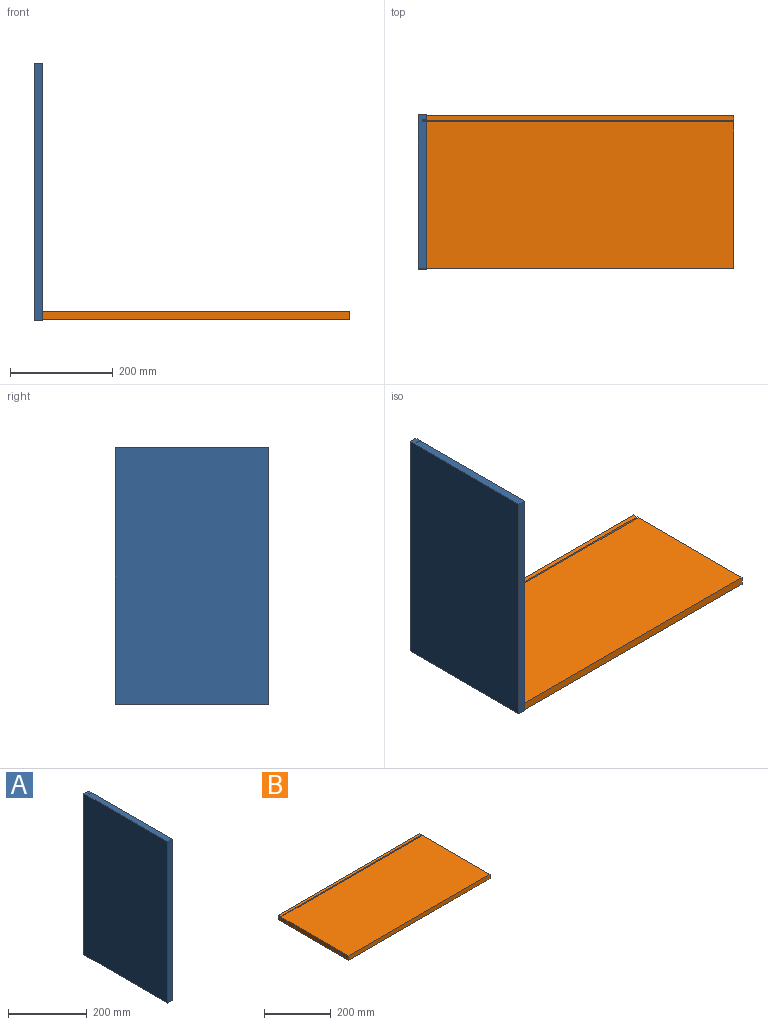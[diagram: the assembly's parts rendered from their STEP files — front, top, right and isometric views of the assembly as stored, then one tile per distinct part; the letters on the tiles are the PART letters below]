
ASSEMBLY  parts=2 mates=1
PART A: 18 faces, bbox 16x300x500 mm
  f0: plane 500x287mm, normal (1,0,0), area 143298.9mm2, adj f1,f3,f6,f8,f10,f12,f14,f16
  f1: plane 300x16mm, normal (0,0,-1), area 4776mm2, adj f0,f2,f4,f5,f6,f7,f8,f9
  f2: plane 500x10mm, normal (1,0,0), area 5000mm2, adj f1,f3,f5,f7
  f3: plane 300x16mm, normal (0,0,1), area 4776mm2, adj f0,f2,f4,f5,f6,f7,f8,f9
  f4: plane 500x300mm, normal (-1,0,0), area 150000mm2, adj f1,f3,f5,f6
  f5: plane 500x16mm, normal (0,1,0), area 8000mm2, adj f1,f2,f3,f4
  f6: plane 500x16mm, normal (0,-1,0), area 8000mm2, adj f0,f1,f3,f4
  f7: plane 500x8mm, normal (0,-1,0), area 4000mm2, adj f1,f2,f3,f9
  f8: plane 500x8mm, normal (0,1,0), area 4000mm2, adj f0,f1,f3,f9
  f9: plane 500x3mm, normal (1,0,0), area 1500mm2, adj f1,f3,f7,f8
  f10: cylinder r=4mm len=12mm, axis (1,0,0), area 301.6mm2, adj f0,f11
  f11: plane 8x8mm, normal (1,0,0), area 50.3mm2, adj f10
  f12: cylinder r=4mm len=12mm, axis (1,0,0), area 301.6mm2, adj f0,f13
  f13: plane 8x8mm, normal (1,0,0), area 50.3mm2, adj f12
  f14: cylinder r=4mm len=12mm, axis (1,0,0), area 301.6mm2, adj f0,f15
  f15: plane 8x8mm, normal (1,0,0), area 50.3mm2, adj f14
  f16: cylinder r=4mm len=12mm, axis (1,0,0), area 301.6mm2, adj f0,f17
  f17: plane 8x8mm, normal (1,0,0), area 50.3mm2, adj f16
PART B: 20 faces, bbox 600x299x16 mm
  f0: plane 600x9.5mm, normal (0,0,1), area 5700mm2, adj f1,f3,f5,f7
  f1: plane 299x16mm, normal (-1,0,0), area 4558.9mm2, adj f0,f2,f4,f5,f6,f7,f8,f9
  f2: plane 600x299mm, normal (0,0,-1), area 179046.6mm2, adj f1,f3,f5,f6,f16,f18
  f3: plane 299x16mm, normal (1,0,0), area 4760mm2, adj f0,f2,f4,f5,f6,f7,f8,f9
  f4: plane 600x286.5mm, normal (0,0,1), area 171900mm2, adj f1,f3,f6,f8
  f5: plane 600x16mm, normal (0,1,0), area 9600mm2, adj f0,f1,f2,f3
  f6: plane 600x16mm, normal (0,-1,0), area 9600mm2, adj f1,f2,f3,f4
  f7: plane 600x8mm, normal (0,-1,0), area 4800mm2, adj f0,f1,f3,f9
  f8: plane 600x8mm, normal (0,1,0), area 4800mm2, adj f1,f3,f4,f9
  f9: plane 600x3mm, normal (0,0,1), area 1800mm2, adj f1,f3,f7,f8
  f10: cylinder r=4mm len=8mm, axis (-1,0,0), area 177.6mm2, adj f1,f18
  f11: cylinder r=4mm len=20mm, axis (-1,0,0), area 502.7mm2, adj f1,f12
  f12: plane 8x8mm, normal (-1,0,0), area 50.3mm2, adj f11
  f13: cylinder r=4mm len=20mm, axis (-1,0,0), area 502.7mm2, adj f1,f14
  f14: plane 8x8mm, normal (-1,0,0), area 50.3mm2, adj f13
  f15: cylinder r=4mm len=8mm, axis (-1,0,0), area 177.6mm2, adj f1,f16
  f16: cylinder r=7.5mm len=15mm, axis (0,0,-1), area 536.7mm2, adj f2,f15,f17
  f17: plane 15x15mm, normal (0,0,-1), area 176.7mm2, adj f16
  f18: cylinder r=7.5mm len=15mm, axis (0,0,-1), area 536.7mm2, adj f2,f10,f19
  f19: plane 15x15mm, normal (0,0,-1), area 176.7mm2, adj f18
PLACE A t=(160.52,0.5,101.78)mm fixed
PLACE B t=(160.52,0.5,101.78)mm
MATE fastened A.f16 <-> B.f15  axis (1,0,0) through (16,37,8.5)mm
